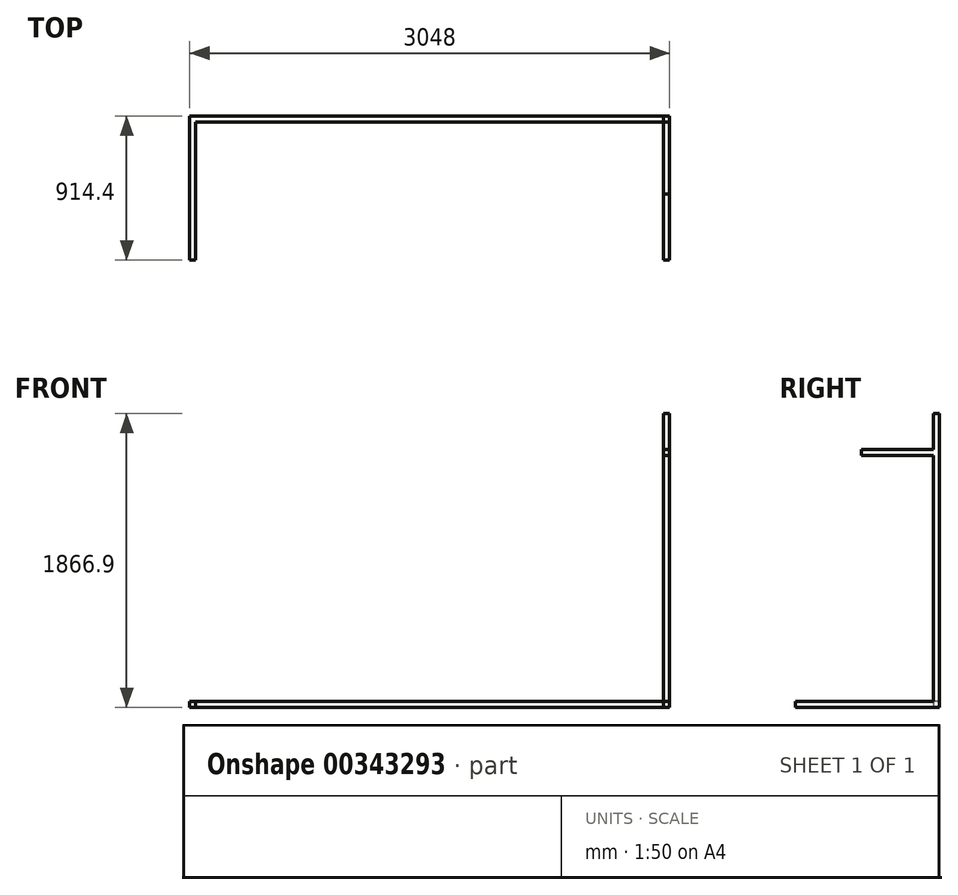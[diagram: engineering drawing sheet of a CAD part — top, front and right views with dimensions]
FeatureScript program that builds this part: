
annotation { "Feature Type Name" : "Feature", "Feature Type Description" : "" }
export const myFeature = defineFeature(function(context is Context, id is Id, definition is map)
    precondition{}
    {
        {
            var Q0;
            Q0=qCreatedBy(makeId("Top.planeOp"),FACE);
            var sketch = newSketch(context, id + "F0", { "sketchPlane" : qUnion([Q0])});
            skLineSegment(sketch, "E0.bottom", {"start": v(1524, 457.2) * mm, "end": v(-1524, 457.2) * mm});
            skLineSegment(sketch, "E0.top", {"start": v(1524, -457.2) * mm, "end": v(-1524, -457.2) * mm});
            skLineSegment(sketch, "E0.left", {"start": v(1524, 457.2) * mm, "end": v(1524, -457.2) * mm});
            skLineSegment(sketch, "E0.right", {"start": v(-1524, 457.2) * mm, "end": v(-1524, -457.2) * mm});
            skPoint(sketch, "E0.middle", {"position": v(0, 0) * mm});
            skLineSegment(sketch, "E1", {"start": v(1524, -457.2) * mm, "end": v(1485.9, -457.2) * mm});
            skLineSegment(sketch, "E2", {"start": v(1485.9, -457.2) * mm, "end": v(1485.9, 419.1) * mm});
            skLineSegment(sketch, "E3", {"start": v(1485.9, 419.1) * mm, "end": v(-1485.9, 419.1) * mm});
            skLineSegment(sketch, "E4", {"start": v(-1485.9, 419.1) * mm, "end": v(-1485.9, -457.2) * mm});
            skSolve(sketch);
        }
        {
            var Q0;
            Q0=makeQuery(id+"F0.imprint","IMPRINT",FACE,{"disambiguationData":[TD([[makeQuery(id+"F0.imprint","IMPRINT",EDGE,{"derivedFrom":sQuery(id+"F0.wireOp",EDGE,"E0.bottom")}),1.0]])]});
            extrude(context, id + "F1", {"entities" : qUnion([Q0]), "depth" : 38.1 * mm});
        }
        {
            var Q0;
            Q0=makeQuery(id+"F1.opExtrude","SWEPT_FACE",FACE,{"disambiguationData":[OSD([sQuery(id+"F0.wireOp",EDGE,"E0.left")])]});
            var sketch = newSketch(context, id + "F2", { "sketchPlane" : qUnion([Q0])});
            skLineSegment(sketch, "E5", {"start": v(457.2, 38.1) * mm, "end": v(457.2, 1866.9) * mm});
            skLineSegment(sketch, "E6", {"start": v(457.2, 1866.9) * mm, "end": v(419.1, 1866.9) * mm});
            skLineSegment(sketch, "E7", {"start": v(419.1, 1866.9) * mm, "end": v(419.1, 38.1) * mm});
            skLineSegment(sketch, "E8", {"start": v(419.1, 1866.9) * mm, "end": v(419.1, 1638.3) * mm});
            skLineSegment(sketch, "E9", {"start": v(419.1, 1638.3) * mm, "end": v(-38.1, 1638.3) * mm});
            skLineSegment(sketch, "E10", {"start": v(-38.1, 1638.3) * mm, "end": v(-38.1, 1600.2) * mm});
            skLineSegment(sketch, "E11", {"start": v(-38.1, 1600.2) * mm, "end": v(419.1, 1600.2) * mm});
            skSolve(sketch);
        }
        {
            var Q0;
            {var subQ0=sQuery(id+"F2.wireOp",EDGE,"E5");Q0=makeQuery(id+"F2.imprint","IMPRINT",FACE,{"disambiguationData":[TD([[makeQuery(id+"F2.imprint","IMPRINT",EDGE,{"derivedFrom":subQ0}),1.0]])]});}
            extrude(context, id + "F3", {"entities" : qUnion([Q0]), "operationType" : NewBodyOperationType.ADD, "oppositeDirection" : true, "depth" : 38.1 * mm});
        }
        {
            var Q0;
            Q0 = qSketchRegion(id + "F2", true);
            extrude(context, id + "F4", {"entities" : qUnion([Q0]), "operationType" : NewBodyOperationType.ADD, "oppositeDirection" : true, "depth" : 38.1 * mm});
        }
    });
